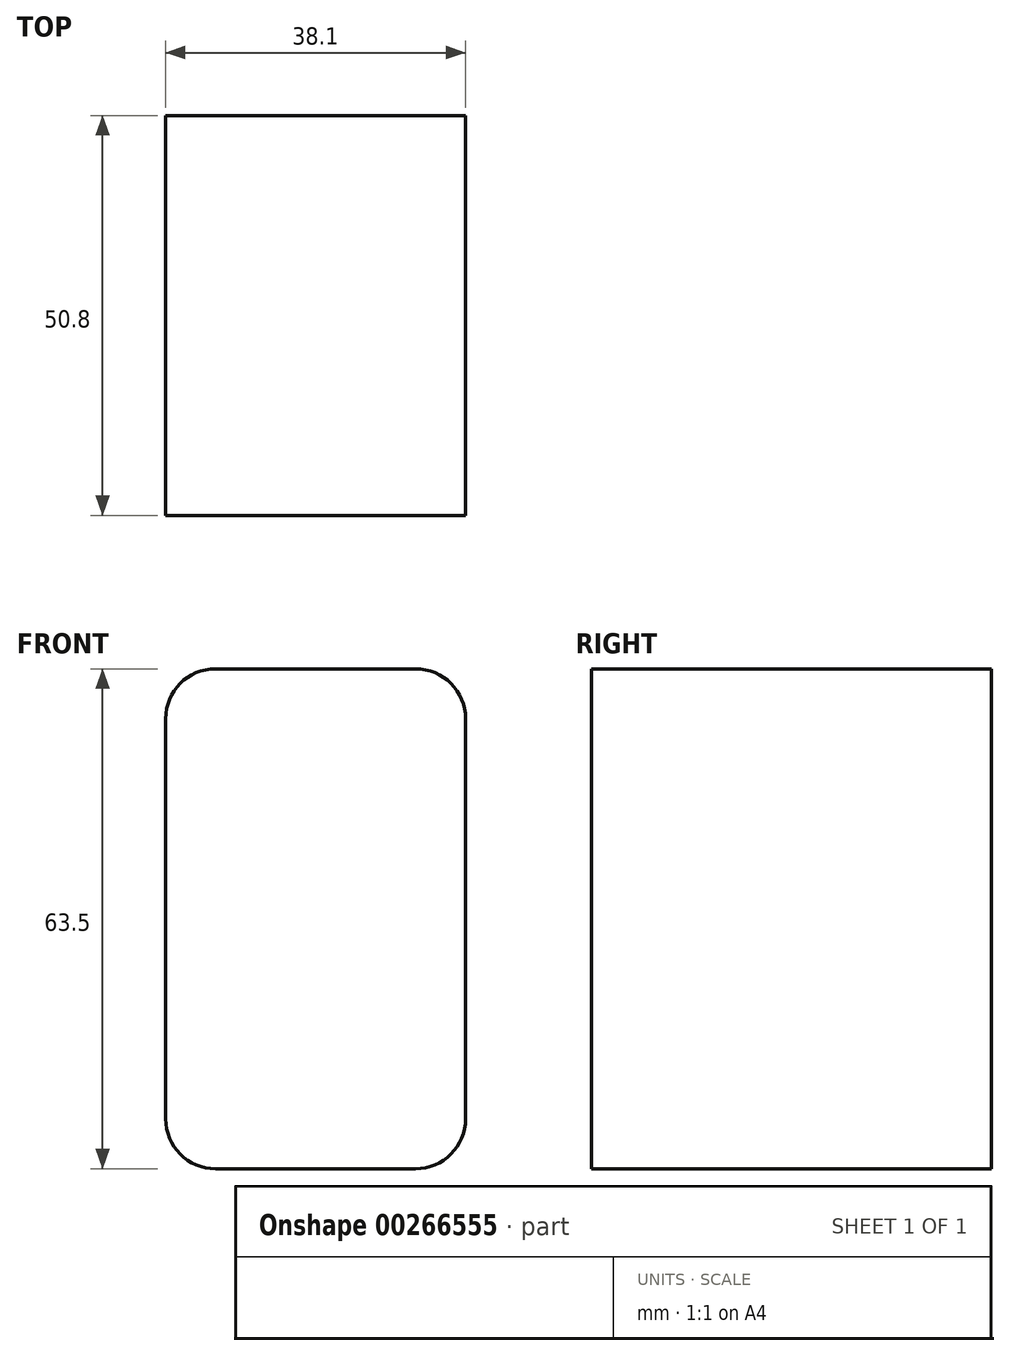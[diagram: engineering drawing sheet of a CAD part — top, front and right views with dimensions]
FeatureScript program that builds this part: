
annotation { "Feature Type Name" : "Feature", "Feature Type Description" : "" }
export const myFeature = defineFeature(function(context is Context, id is Id, definition is map)
    precondition{}
    {
        {
            var Q0;
            Q0=qCreatedBy(makeId("Front.planeOp"),FACE);
            var sketch = newSketch(context, id + "F0", { "sketchPlane" : qUnion([Q0])});
            skLineSegment(sketch, "E0.bottom", {"start": v(-83.95, 43.48) * mm, "end": v(-58.55, 43.48) * mm});
            skLineSegment(sketch, "E0.top", {"start": v(-83.95, -20.02) * mm, "end": v(-58.55, -20.02) * mm});
            skLineSegment(sketch, "E0.left", {"start": v(-90.3, 37.13) * mm, "end": v(-90.3, -13.67) * mm});
            skLineSegment(sketch, "E0.right", {"start": v(-52.2, 37.13) * mm, "end": v(-52.2, -13.67) * mm});
            skPoint(sketch, "E1.visualSharp", {"position": v(-90.3, 43.48) * mm});
            skArc(sketch, "E1.filletArc", {"start": v(-83.95, 43.48) * mm, "mid": v(-88.44, 41.62) * mm, "end": v(-90.3, 37.13) * mm});
            skPoint(sketch, "E2.visualSharp", {"position": v(-52.2, -20.02) * mm});
            skArc(sketch, "E2.filletArc", {"start": v(-58.55, -20.02) * mm, "mid": v(-54.06, -18.16) * mm, "end": v(-52.2, -13.67) * mm});
            skPoint(sketch, "E3.visualSharp", {"position": v(-52.2, 43.48) * mm});
            skArc(sketch, "E3.filletArc", {"start": v(-52.2, 37.13) * mm, "mid": v(-54.06, 41.62) * mm, "end": v(-58.55, 43.48) * mm});
            skPoint(sketch, "E4.visualSharp", {"position": v(-90.3, -20.02) * mm});
            skArc(sketch, "E4.filletArc", {"start": v(-90.3, -13.67) * mm, "mid": v(-88.44, -18.16) * mm, "end": v(-83.95, -20.02) * mm});
            skSolve(sketch);
        }
        {
            var Q0;
            Q0=makeQuery(id+"F0.imprint","IMPRINT",FACE,{"disambiguationData":[TD([[makeQuery(id+"F0.imprint","IMPRINT",EDGE,{"derivedFrom":sQuery(id+"F0.wireOp",EDGE,"E0.bottom")}),-1.0]])]});
            var Q1;
            Q1=sQuery(id+"F0.wireOp",EDGE,"E0.left");
            var Q2;
            Q2=sQuery(id+"F0.wireOp",EDGE,"E0.top");
            var Q3;
            Q3=sQuery(id+"F0.wireOp",EDGE,"E0.right");
            var Q4;
            Q4=sQuery(id+"F0.wireOp",EDGE,"E0.bottom");
            extrude(context, id + "F1", {"entities" : qUnion([Q0]), "surfaceEntities" : qUnion([Q1, Q2, Q3, Q4]), "depth" : 50.8 * mm});
        }
    });
